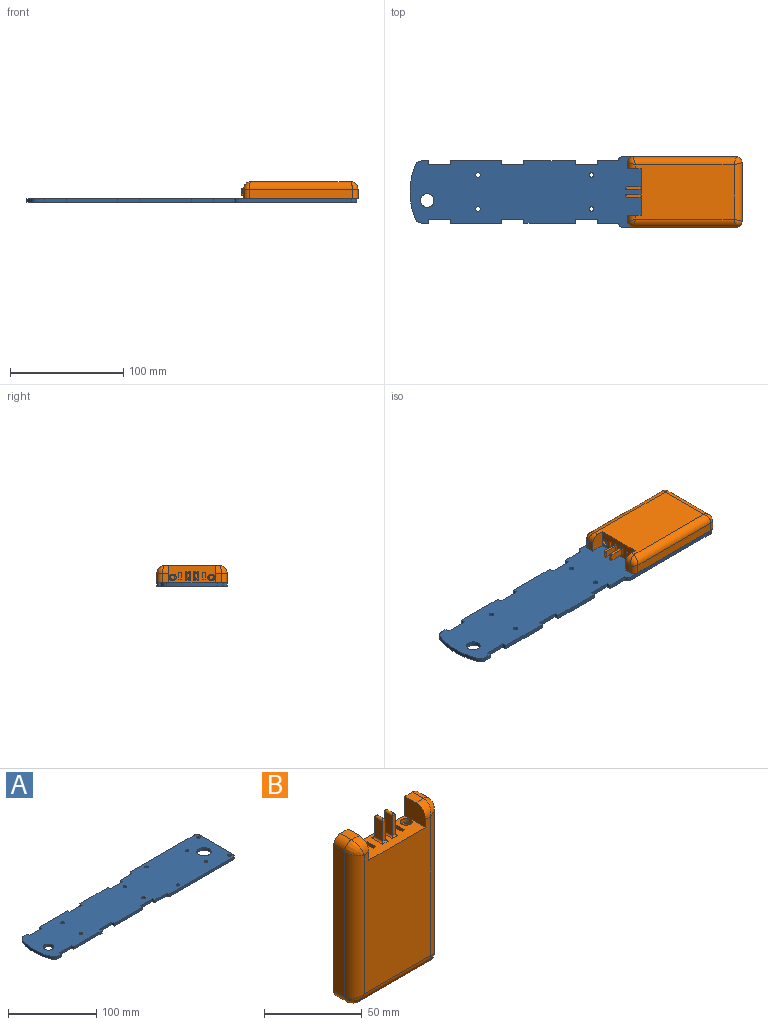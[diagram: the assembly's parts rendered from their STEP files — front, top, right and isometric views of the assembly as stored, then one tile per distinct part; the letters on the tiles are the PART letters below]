
ASSEMBLY  parts=2 mates=1
PART A: 52 faces, bbox 292x62x3.5 mm
  f0: cylinder r=66.02mm len=45.86mm, axis (0,0,-1), area 163.9mm2, adj f1,f45,f46,f47
  f1: cylinder r=7mm len=6.56mm, axis (0,0,-1), area 29.8mm2, adj f0,f2,f46,f47
  f2: plane 5.33x3.5mm, normal (0,-1,0), area 18.6mm2, adj f1,f3,f46,f47
  f3: plane 3.6x3.5mm, normal (1,0,0), area 12.6mm2, adj f2,f4,f46,f47
  f4: plane 19.5x3.5mm, normal (0,-1,0), area 68.2mm2, adj f3,f5,f46,f47
  f5: plane 3.6x3.5mm, normal (-1,0,0), area 12.6mm2, adj f4,f6,f46,f47
  f6: plane 45.57x3.5mm, normal (0,-1,0), area 159.5mm2, adj f5,f7,f46,f47
  f7: plane 3.6x3.5mm, normal (1,0,0), area 12.6mm2, adj f6,f8,f46,f47
  f8: plane 19.5x3.5mm, normal (0,-1,0), area 68.3mm2, adj f7,f9,f46,f47
  f9: plane 3.6x3.5mm, normal (-1,0,0), area 12.6mm2, adj f8,f10,f46,f47
  f10: plane 45.4x3.5mm, normal (0,-1,0), area 158.9mm2, adj f9,f11,f46,f47
  f11: plane 3.6x3.5mm, normal (1,0,0), area 12.6mm2, adj f10,f12,f46,f47
  f12: plane 19.5x3.5mm, normal (0,-1,0), area 68.3mm2, adj f11,f13,f46,f47
  f13: plane 3.6x3.5mm, normal (-1,0,0), area 12.6mm2, adj f12,f14,f46,f47
  f14: plane 18.7x3.5mm, normal (0,-1,0), area 65.5mm2, adj f13,f15,f46,f47
  f15: plane 3.5x0.5mm, normal (-1,0,0), area 1.8mm2, adj f14,f46,f47,f48
  f16: plane 99.83x3.5mm, normal (0,-1,0), area 349.4mm2, adj f46,f47,f48,f50
  f17: plane 52x3.5mm, normal (1,0,0), area 182mm2, adj f46,f47,f50,f51
  f18: plane 100x3.5mm, normal (0,1,0), area 350mm2, adj f46,f47,f49,f51
  f19: plane 3.5x0.5mm, normal (-1,0,0), area 1.8mm2, adj f20,f46,f47,f49
  f20: plane 18.7x3.5mm, normal (0,1,0), area 65.5mm2, adj f19,f21,f46,f47
  f21: plane 3.6x3.5mm, normal (-1,0,0), area 12.6mm2, adj f20,f22,f46,f47
  f22: plane 19.5x3.5mm, normal (0,1,0), area 68.2mm2, adj f21,f23,f46,f47
  f23: plane 3.6x3.5mm, normal (1,0,0), area 12.6mm2, adj f22,f24,f46,f47
  f24: plane 45.4x3.5mm, normal (0,1,0), area 158.9mm2, adj f23,f25,f46,f47
  f25: plane 3.6x3.5mm, normal (-1,0,0), area 12.6mm2, adj f24,f26,f46,f47
  f26: plane 19.5x3.5mm, normal (0,1,0), area 68.2mm2, adj f25,f27,f46,f47
  f27: plane 3.6x3.5mm, normal (1,0,0), area 12.6mm2, adj f26,f28,f46,f47
  f28: plane 45.4x3.5mm, normal (0,1,0), area 158.9mm2, adj f27,f29,f46,f47
  f29: plane 3.6x3.5mm, normal (-1,0,0), area 12.6mm2, adj f28,f30,f46,f47
  f30: plane 19.5x3.5mm, normal (0,1,0), area 68.2mm2, adj f29,f31,f46,f47
  f31: plane 3.6x3.5mm, normal (1,0,0), area 12.6mm2, adj f30,f32,f46,f47
  f32: plane 5.33x3.5mm, normal (0,1,0), area 18.6mm2, adj f31,f45,f46,f47
  f33: cylinder r=6mm len=12mm, axis (0,0,-1), area 131.9mm2, adj f46,f47
  f34: cylinder r=2mm len=4mm, axis (0,0,-1), area 44mm2, adj f46,f47
  f35: cylinder r=2mm len=4mm, axis (0,0,-1), area 44mm2, adj f46,f47
  f36: cylinder r=2mm len=4mm, axis (0,0,-1), area 44mm2, adj f46,f47
  f37: cylinder r=2mm len=4mm, axis (0,0,-1), area 44mm2, adj f46,f47
  f38: cylinder r=2mm len=4mm, axis (0,0,-1), area 44mm2, adj f46,f47
  f39: cylinder r=2mm len=4mm, axis (0,0,-1), area 44mm2, adj f46,f47
  f40: cylinder r=2mm len=4mm, axis (0,0,-1), area 44mm2, adj f46,f47
  f41: cylinder r=2mm len=4mm, axis (0,0,-1), area 44mm2, adj f46,f47
  f42: cylinder r=2mm len=4mm, axis (0,0,-1), area 44mm2, adj f46,f47
  f43: cylinder r=2mm len=4mm, axis (0,0,-1), area 44mm2, adj f46,f47
  f44: cylinder r=8mm len=16mm, axis (0,0,-1), area 175.9mm2, adj f46,f47
  f45: cylinder r=7mm len=6.56mm, axis (0,0,-1), area 29.8mm2, adj f0,f32,f46,f47
  f46: plane 292x62mm, normal (0,0,1), area 15823.9mm2, adj f0,f1,f2,f3,f4,f5,f6,f7
  f47: plane 292x62mm, normal (0,0,-1), area 15823.9mm2, adj f0,f1,f2,f3,f4,f5,f6,f7
  f48: cylinder r=3mm len=3.5mm, axis (0,0,1), area 16.5mm2, adj f15,f16,f46,f47
  f49: cylinder r=3mm len=3.5mm, axis (0,0,1), area 16.5mm2, adj f18,f19,f46,f47
  f50: cylinder r=5mm len=5mm, axis (0,0,1), area 27.5mm2, adj f16,f17,f46,f47
  f51: cylinder r=5mm len=5mm, axis (0,0,-1), area 27.5mm2, adj f17,f18,f46,f47
PART B: 90 faces, bbox 62x15x103 mm
  f0: cylinder r=2mm len=7.5mm, axis (0,0,1), area 94.2mm2, adj f49,f69
  f1: cylinder r=2mm len=7.5mm, axis (0,0,1), area 94.2mm2, adj f47,f67
  f2: plane 63x49.6mm, normal (0,1,0), area 3000.5mm2, adj f71,f72,f73,f74,f76,f77,f78,f79
  f3: plane 69x8.8mm, normal (-1,0,0), area 607.2mm2, adj f6,f45,f49,f74
  f4: plane 23.6x8.8mm, normal (0,0,-1), area 184.5mm2, adj f6,f7,f8,f9,f10,f11,f14,f48
  f5: plane 67x8.8mm, normal (1,0,0), area 589.6mm2, adj f6,f47,f53,f71
  f6: plane 101x62mm, normal (0,1,0), area 1512.6mm2, adj f3,f4,f5,f16,f25,f26,f27,f28
  f7: plane 6x6mm, normal (1,0,0), area 36mm2, adj f4,f8,f13,f16,f78
  f8: plane 6x2mm, normal (0,-1,0), area 12mm2, adj f4,f7,f9,f16
  f9: plane 6x6mm, normal (-1,0,0), area 36mm2, adj f4,f8,f13,f16,f78
  f10: plane 6x2mm, normal (0,-1,0), area 12mm2, adj f4,f11,f14,f16
  f11: plane 6x6mm, normal (-1,0,0), area 36mm2, adj f4,f10,f12,f16,f78
  f12: plane 6x2mm, normal (0,1,0), area 12mm2, adj f11,f14,f16,f78
  f13: plane 6x2mm, normal (0,1,0), area 12mm2, adj f7,f9,f16,f78
  f14: plane 6x6mm, normal (1,0,0), area 36mm2, adj f4,f10,f12,f16,f78
  f15: plane 87x48mm, normal (0,-1,0), area 3971mm2, adj f16,f25,f28,f81,f83,f85,f87,f89
  f16: plane 41x15mm, normal (0,0,1), area 470.5mm2, adj f6,f7,f8,f9,f10,f11,f12,f13
  f17: plane 12x2mm, normal (0,-1,0), area 24mm2, adj f18,f20,f34,f43
  f18: plane 12x6mm, normal (-1,0,0), area 72mm2, adj f17,f19,f35,f44
  f19: plane 12x2mm, normal (0,1,0), area 24mm2, adj f18,f20,f36,f42
  f20: plane 12x6mm, normal (1,0,0), area 72mm2, adj f17,f19,f35,f41
  f21: plane 12x6mm, normal (1,0,0), area 72mm2, adj f22,f24,f32,f39
  f22: plane 12x2mm, normal (0,-1,0), area 24mm2, adj f21,f23,f33,f40
  f23: plane 12x6mm, normal (-1,0,0), area 72mm2, adj f22,f24,f32,f38
  f24: plane 12x2mm, normal (0,1,0), area 24mm2, adj f21,f23,f31,f37
  f25: plane 15x12mm, normal (-1,0,0), area 169.5mm2, adj f6,f15,f16,f27,f81
  f26: plane 91x8mm, normal (1,0,0), area 728mm2, adj f6,f54,f56,f83
  f27: plane 8x5.5mm, normal (0,0,1), area 44mm2, adj f6,f25,f56,f81
  f28: plane 15x12mm, normal (1,0,0), area 169.5mm2, adj f6,f15,f16,f30,f89
  f29: plane 91x8mm, normal (-1,0,0), area 728mm2, adj f6,f55,f57,f87
  f30: plane 8x5.5mm, normal (0,0,1), area 44mm2, adj f6,f28,f57,f89
  f31: cylinder r=1mm len=2mm, axis (1,0,0), area 2mm2, adj f24,f32
  f32: cylinder r=1mm len=6mm, axis (0,1,0), area 16.6mm2, adj f21,f23,f31,f33
  f33: cylinder r=1mm len=2mm, axis (-1,0,0), area 2mm2, adj f22,f32
  f34: cylinder r=1mm len=2mm, axis (-1,0,0), area 2mm2, adj f17,f35
  f35: cylinder r=1mm len=6mm, axis (0,-1,0), area 16.6mm2, adj f18,f20,f34,f36
  f36: cylinder r=1mm len=2mm, axis (1,0,0), area 2mm2, adj f19,f35
  f37: cylinder r=1mm len=4mm, axis (-1,0,0), area 4.3mm2, adj f16,f24,f38,f39
  f38: cylinder r=1mm len=8mm, axis (0,-1,0), area 10.6mm2, adj f16,f23,f37,f40
  f39: cylinder r=1mm len=8mm, axis (0,1,0), area 10.6mm2, adj f16,f21,f37,f40
  f40: cylinder r=1mm len=4mm, axis (1,0,0), area 4.3mm2, adj f16,f22,f38,f39
  f41: cylinder r=1mm len=8mm, axis (0,1,0), area 10.6mm2, adj f16,f20,f42,f43
  f42: cylinder r=1mm len=4mm, axis (-1,0,0), area 4.3mm2, adj f16,f19,f41,f44
  f43: cylinder r=1mm len=4mm, axis (1,0,0), area 4.3mm2, adj f16,f17,f41,f44
  f44: cylinder r=1mm len=8mm, axis (0,-1,0), area 10.6mm2, adj f16,f18,f42,f43
  f45: plane 57.6x8.8mm, normal (0,0,1), area 506.9mm2, adj f3,f6,f53,f72
  f46: plane 52x8mm, normal (0,0,-1), area 416mm2, adj f6,f54,f55,f85
  f47: plane 16x8.8mm, normal (0,0,-1), area 128.2mm2, adj f1,f5,f6,f51,f73
  f48: plane 8.8x2mm, normal (1,0,0), area 17.6mm2, adj f4,f6,f51,f75
  f49: plane 16x8.8mm, normal (0,0,-1), area 128.2mm2, adj f0,f3,f6,f52,f77
  f50: plane 8.8x2mm, normal (-1,0,0), area 17.6mm2, adj f4,f6,f52,f80
  f51: cylinder r=2mm len=8.8mm, axis (0,1,0), area 27.6mm2, adj f6,f47,f48,f76
  f52: cylinder r=2mm len=8.8mm, axis (0,1,0), area 27.6mm2, adj f6,f49,f50,f79
  f53: cylinder r=2mm len=8.8mm, axis (0,1,0), area 27.6mm2, adj f5,f6,f45,f70
  f54: cylinder r=5mm len=8mm, axis (0,-1,0), area 62.8mm2, adj f6,f26,f46,f84
  f55: cylinder r=5mm len=8mm, axis (0,1,0), area 62.8mm2, adj f6,f29,f46,f86
  f56: cylinder r=5mm len=8mm, axis (0,-1,0), area 62.8mm2, adj f6,f26,f27,f82
  f57: cylinder r=5mm len=8mm, axis (0,1,0), area 62.8mm2, adj f6,f29,f30,f88
  f58: cylinder r=1.5mm len=8mm, axis (0,1,0), area 75.4mm2, adj f6,f59
  f59: plane 3x3mm, normal (0,1,0), area 7.1mm2, adj f58
  f60: cylinder r=1.5mm len=8mm, axis (0,1,0), area 75.4mm2, adj f6,f61
  f61: plane 3x3mm, normal (0,1,0), area 7.1mm2, adj f60
  f62: cylinder r=1.5mm len=8mm, axis (0,1,0), area 75.4mm2, adj f6,f63
  f63: plane 3x3mm, normal (0,1,0), area 7.1mm2, adj f62
  f64: cylinder r=1.5mm len=8mm, axis (0,1,0), area 75.4mm2, adj f6,f65
  f65: plane 3x3mm, normal (0,1,0), area 7.1mm2, adj f64
  f66: cylinder r=3mm len=6mm, axis (0,0,1), area 47.1mm2, adj f16,f67
  f67: plane 6x6mm, normal (0,0,1), area 15.7mm2, adj f1,f66
  f68: cylinder r=3mm len=6mm, axis (0,0,1), area 47.1mm2, adj f16,f69
  f69: plane 6x6mm, normal (0,0,1), area 15.7mm2, adj f0,f68
  f70: bspline ~5.91x5mm, area 16.7mm2, adj f53,f71,f72
  f71: cylinder r=5mm len=67mm, axis (0,0,-1), area 503.4mm2, adj f2,f5,f70,f73
  f72: cylinder r=5mm len=57.6mm, axis (-1,0,0), area 429.6mm2, adj f2,f45,f70,f74
  f73: cylinder r=5mm len=16mm, axis (-1,0,0), area 111.4mm2, adj f2,f47,f71,f76
  f74: cylinder r=5mm len=69mm, axis (0,0,1), area 513.4mm2, adj f2,f3,f72,f77
  f75: cylinder r=5mm len=4mm, axis (0,0,1), area 6.1mm2, adj f48,f76,f78
  f76: torus R=7mm, axis (0,1,0), area 42.3mm2, adj f2,f51,f73,f75,f78
  f77: cylinder r=5mm len=16mm, axis (-1,0,0), area 111.4mm2, adj f2,f49,f74,f79
  f78: cylinder r=5mm len=23.6mm, axis (-1,0,0), area 157.8mm2, adj f2,f4,f7,f9,f11,f12,f13,f14
  f79: torus R=7mm, axis (0,1,0), area 42.3mm2, adj f2,f52,f77,f78,f80
  f80: cylinder r=5mm len=4mm, axis (0,0,1), area 6.1mm2, adj f50,f78,f79
  f81: cylinder r=7mm len=7mm, axis (1,0,0), area 52.5mm2, adj f15,f25,f27,f82
  f82: bspline ~8.55x7mm, area 56.6mm2, adj f56,f81,f83
  f83: cylinder r=7mm len=91mm, axis (0,0,1), area 984.6mm2, adj f15,f26,f82,f84
  f84: bspline ~7.39x7mm, area 56.6mm2, adj f54,f83,f85
  f85: cylinder r=7mm len=52mm, axis (-1,0,0), area 555.8mm2, adj f15,f46,f84,f86
  f86: bspline ~8.55x7mm, area 56.6mm2, adj f55,f85,f87
  f87: cylinder r=7mm len=91mm, axis (0,0,-1), area 984.6mm2, adj f15,f29,f86,f88
  f88: bspline ~7.39x7mm, area 56.6mm2, adj f57,f87,f89
  f89: cylinder r=7mm len=7mm, axis (-1,0,0), area 52.5mm2, adj f15,f28,f30,f88
PLACE A at identity fixed
PLACE B rot(axis=(-0.58,-0.58,0.58),120deg) t=(140,0,11)mm
MATE slider A.f37 <-> B.f64  axis (0,0,1) through (135,-25,3.5)mm
